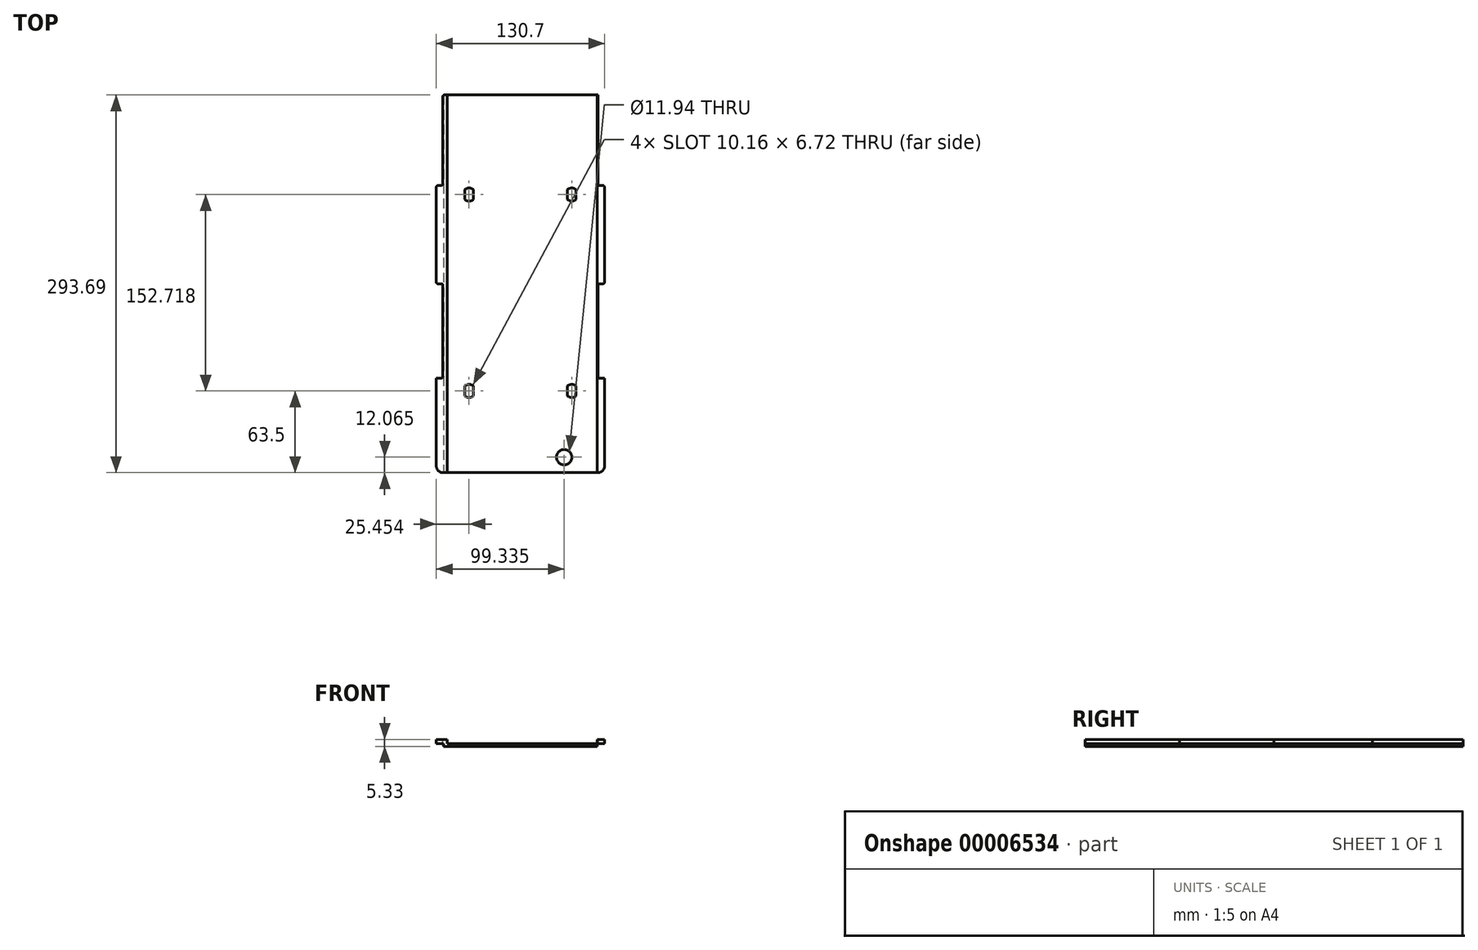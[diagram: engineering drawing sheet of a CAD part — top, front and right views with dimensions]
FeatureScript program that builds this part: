
annotation { "Feature Type Name" : "Feature", "Feature Type Description" : "" }
export const myFeature = defineFeature(function(context is Context, id is Id, definition is map)
    precondition{}
    {
        {
            var Q0;
            Q0=qCreatedBy(makeId("Front.planeOp"),FACE);
            var sketch = newSketch(context, id + "F0", { "sketchPlane" : qUnion([Q0])});
            skLineSegment(sketch, "E0.bottom", {"start": v(0, 0) * mm, "end": v(119.38, 0) * mm});
            skLineSegment(sketch, "E0.top", {"start": v(0, 2.16) * mm, "end": v(119.38, 2.16) * mm});
            skLineSegment(sketch, "E0.left", {"start": v(0, 0) * mm, "end": v(0, 2.16) * mm});
            skLineSegment(sketch, "E0.right", {"start": v(119.38, 0) * mm, "end": v(119.38, 2.16) * mm});
            skLineSegment(sketch, "E1", {"start": v(2.72, 2.16) * mm, "end": v(2.72, 5.33) * mm});
            skLineSegment(sketch, "E2", {"start": v(2.72, 5.33) * mm, "end": v(0, 5.33) * mm});
            skLineSegment(sketch, "E3", {"start": v(0, 5.33) * mm, "end": v(0, 2.16) * mm});
            skLineSegment(sketch, "E4.bottom", {"start": v(119.38, 2.16) * mm, "end": v(116.66, 2.16) * mm});
            skLineSegment(sketch, "E4.top", {"start": v(119.38, 5.33) * mm, "end": v(116.66, 5.33) * mm});
            skLineSegment(sketch, "E4.left", {"start": v(119.38, 2.16) * mm, "end": v(119.38, 5.33) * mm});
            skLineSegment(sketch, "E4.right", {"start": v(116.66, 2.16) * mm, "end": v(116.66, 5.33) * mm});
            skLineSegment(sketch, "E5.bottom", {"start": v(119.38, 5.33) * mm, "end": v(125.04, 5.33) * mm});
            skLineSegment(sketch, "E5.top", {"start": v(119.38, 2.16) * mm, "end": v(125.04, 2.16) * mm});
            skLineSegment(sketch, "E5.left", {"start": v(119.38, 5.33) * mm, "end": v(119.38, 2.16) * mm});
            skLineSegment(sketch, "E5.right", {"start": v(125.04, 5.33) * mm, "end": v(125.04, 2.16) * mm});
            skLineSegment(sketch, "E6.bottom", {"start": v(0, 5.33) * mm, "end": v(-5.66, 5.33) * mm});
            skLineSegment(sketch, "E6.top", {"start": v(0, 2.16) * mm, "end": v(-5.66, 2.16) * mm});
            skLineSegment(sketch, "E6.right", {"start": v(-5.66, 5.33) * mm, "end": v(-5.66, 2.16) * mm});
            skSolve(sketch);
        }
        {
            var Q0;
            Q0=makeQuery(id+"F0.imprint","IMPRINT",FACE,{"disambiguationData":[TD([[makeQuery(id+"F0.imprint","IMPRINT",EDGE,{"derivedFrom":sQuery(id+"F0.wireOp",EDGE,"E5.bottom")}),-1.0]])]});
            var Q1;
            Q1=makeQuery(id+"F0.imprint","IMPRINT",FACE,{"disambiguationData":[TD([[makeQuery(id+"F0.imprint","IMPRINT",EDGE,{"derivedFrom":sQuery(id+"F0.wireOp",EDGE,"E6.bottom")}),1.0]])]});
            var Q2;
            Q2=makeQuery(id+"F0.imprint","IMPRINT",FACE,{"disambiguationData":[TD([[makeQuery(id+"F0.imprint","IMPRINT",EDGE,{"derivedFrom":sQuery(id+"F0.wireOp",EDGE,"E0.bottom")}),1.0]])]});
            var Q3;
            {var subQ1=sQuery(id+"F0.wireOp",EDGE,"E1");Q3=makeQuery(id+"F0.imprint","IMPRINT",FACE,{"disambiguationData":[TD([[makeQuery(id+"F0.imprint","IMPRINT",EDGE,{"derivedFrom":subQ1}),1.0]])]});}
            var Q4;
            Q4=makeQuery(id+"F0.imprint","IMPRINT",FACE,{"disambiguationData":[TD([[makeQuery(id+"F0.imprint","IMPRINT",EDGE,{"derivedFrom":sQuery(id+"F0.wireOp",EDGE,"E4.bottom")}),-1.0]])]});
            extrude(context, id + "F1", {"entities" : qUnion([Q0, Q1, Q2, Q3, Q4]), "oppositeDirection" : true, "depth" : 293.7 * mm});
        }
        {
            var Q0;
            Q0=makeQuery(id+"F1.opExtrude","CAP_EDGE",EDGE,{"disambiguationData":[OSD([sQuery(id+"F0.wireOp",EDGE,"E5.right")])],"isStart":true});
            var Q1;
            Q1=makeQuery(id+"F1.opExtrude","CAP_EDGE",EDGE,{"disambiguationData":[OSD([sQuery(id+"F0.wireOp",EDGE,"E6.right")])],"isStart":true});
            var Q2;
            Q2=makeQuery(id+"F1.opExtrude","CAP_EDGE",EDGE,{"disambiguationData":[OSD([sQuery(id+"F0.wireOp",EDGE,"E5.right")])],"isStart":false});
            var Q3;
            Q3=makeQuery(id+"F1.opExtrude","CAP_EDGE",EDGE,{"disambiguationData":[OSD([sQuery(id+"F0.wireOp",EDGE,"E6.right")])],"isStart":false});
            fillet(context, id + "F2", {"entities" : qUnion([Q0, Q1, Q2, Q3]), "radius" : 5.08 * mm, "tangentPropagation" : true, "allowEdgeOverflow" : false});
        }
        {
            var Q0;
            Q0=makeQuery(id+"F1.opExtrude","SWEPT_FACE",FACE,{"disambiguationData":[OSD([sQuery(id+"F0.wireOp",EDGE,"E0.top")])]});
            var sketch = newSketch(context, id + "F3", { "sketchPlane" : qUnion([Q0])});
            skCircle(sketch, "E7", {"center": v(93.68, 12.06) * mm, "radius": 5.97 * mm});
            skSolve(sketch);
        }
        {
            var Q0;
            Q0=makeQuery(id+"F3.imprint","IMPRINT",FACE,{"disambiguationData":[TD([[makeQuery(id+"F3.imprint","IMPRINT",EDGE,{"derivedFrom":sQuery(id+"F3.wireOp",EDGE,"E7")}),1.0]])]});
            extrude(context, id + "F4", {"entities" : qUnion([Q0]), "operationType" : NewBodyOperationType.REMOVE, "endBound" : BoundingType.THROUGH_ALL, "oppositeDirection" : true, "depth" : 25.4 * mm});
        }
        {
            var Q0;
            Q0=makeQuery(id+"F1.opExtrude","SWEPT_FACE",FACE,{"disambiguationData":[OSD([sQuery(id+"F0.wireOp",EDGE,"E0.top")])]});
            var sketch = newSketch(context, id + "F5", { "sketchPlane" : qUnion([Q0])});
            skArc(sketch, "E8", {"start": v(16.43, 59.69) * mm, "mid": v(19.8, 58.42) * mm, "end": v(23.15, 59.69) * mm});
            skArc(sketch, "E9", {"start": v(96.23, 59.69) * mm, "mid": v(99.59, 58.42) * mm, "end": v(102.95, 59.69) * mm});
            skArc(sketch, "E10", {"start": v(96.23, 212.4) * mm, "mid": v(99.59, 211.14) * mm, "end": v(102.95, 212.4) * mm});
            skArc(sketch, "E11", {"start": v(16.43, 212.4) * mm, "mid": v(19.8, 211.14) * mm, "end": v(23.15, 212.4) * mm});
            skLineSegment(sketch, "E12", {"start": v(23.15, 59.69) * mm, "end": v(23.15, 67.3) * mm});
            skLineSegment(sketch, "E13", {"start": v(16.43, 67.31) * mm, "end": v(16.43, 59.69) * mm});
            skLineSegment(sketch, "E14", {"start": v(16.43, 212.4) * mm, "end": v(16.43, 220.03) * mm});
            skLineSegment(sketch, "E15", {"start": v(23.15, 212.4) * mm, "end": v(23.15, 220.03) * mm});
            skLineSegment(sketch, "E16", {"start": v(96.23, 212.4) * mm, "end": v(96.23, 220.03) * mm});
            skLineSegment(sketch, "E17", {"start": v(102.95, 212.4) * mm, "end": v(102.95, 220.03) * mm});
            skLineSegment(sketch, "E18", {"start": v(96.23, 59.69) * mm, "end": v(96.23, 67.31) * mm});
            skLineSegment(sketch, "E19", {"start": v(102.95, 59.69) * mm, "end": v(102.95, 67.31) * mm});
            skArc(sketch, "E20.trimOffspring", {"start": v(23.15, 67.3) * mm, "mid": v(19.8, 68.58) * mm, "end": v(16.43, 67.31) * mm});
            skArc(sketch, "E21.trimOffspring", {"start": v(23.15, 220.03) * mm, "mid": v(19.8, 221.3) * mm, "end": v(16.43, 220.03) * mm});
            skArc(sketch, "E22.trimOffspring", {"start": v(102.95, 220.03) * mm, "mid": v(99.59, 221.3) * mm, "end": v(96.23, 220.03) * mm});
            skArc(sketch, "E23.trimOffspring", {"start": v(102.95, 67.31) * mm, "mid": v(99.59, 68.58) * mm, "end": v(96.23, 67.3) * mm});
            skSolve(sketch);
        }
        {
            var Q0;
            Q0=makeQuery(id+"F5.imprint","IMPRINT",FACE,{"disambiguationData":[TD([[makeQuery(id+"F5.imprint","IMPRINT",EDGE,{"derivedFrom":sQuery(id+"F5.wireOp",EDGE,"E8")}),1.0]])]});
            var Q1;
            Q1=makeQuery(id+"F5.imprint","IMPRINT",FACE,{"disambiguationData":[TD([[makeQuery(id+"F5.imprint","IMPRINT",EDGE,{"derivedFrom":sQuery(id+"F5.wireOp",EDGE,"E9")}),1.0]])]});
            var Q2;
            Q2=makeQuery(id+"F5.imprint","IMPRINT",FACE,{"disambiguationData":[TD([[makeQuery(id+"F5.imprint","IMPRINT",EDGE,{"derivedFrom":sQuery(id+"F5.wireOp",EDGE,"E11")}),1.0]])]});
            var Q3;
            Q3=makeQuery(id+"F5.imprint","IMPRINT",FACE,{"disambiguationData":[TD([[makeQuery(id+"F5.imprint","IMPRINT",EDGE,{"derivedFrom":sQuery(id+"F5.wireOp",EDGE,"E10")}),1.0]])]});
            extrude(context, id + "F6", {"entities" : qUnion([Q0, Q1, Q2, Q3]), "operationType" : NewBodyOperationType.REMOVE, "endBound" : BoundingType.THROUGH_ALL, "oppositeDirection" : true, "depth" : 25.4 * mm});
        }
        {
            var Q0;
            Q0=makeQuery(id+"F1.opExtrude","SWEPT_FACE",FACE,{"disambiguationData":[OSD([sQuery(id+"F0.wireOp",EDGE,"E2"),sQuery(id+"F0.wireOp",EDGE,"E6.bottom")])]});
            var sketch = newSketch(context, id + "F7", { "sketchPlane" : qUnion([Q0])});
            skLineSegment(sketch, "E24", {"start": v(-5.66, 146.84) * mm, "end": v(125.04, 146.84) * mm, "construction": true});
            skLineSegment(sketch, "E25", {"start": v(59.69, 146.84) * mm, "end": v(59.69, 299.61) * mm, "construction": true});
            skLineSegment(sketch, "E26", {"start": v(59.69, 223.23) * mm, "end": v(-5.66, 223.23) * mm, "construction": true});
            skLineSegment(sketch, "E27.bottom", {"start": v(-5.66, 223.23) * mm, "end": v(-0.58, 223.23) * mm});
            skLineSegment(sketch, "E27.top", {"start": v(-5.66, 293.69) * mm, "end": v(-0.58, 293.69) * mm});
            skLineSegment(sketch, "E27.left", {"start": v(-5.66, 223.23) * mm, "end": v(-5.66, 293.69) * mm});
            skLineSegment(sketch, "E27.right", {"start": v(-0.58, 223.23) * mm, "end": v(-0.58, 293.69) * mm});
            skLineSegment(sketch, "E28.0.MirrorCS", {"start": v(119.96, 223.23) * mm, "end": v(119.96, 293.69) * mm});
            skLineSegment(sketch, "E29.0.MirrorCS", {"start": v(125.04, 223.23) * mm, "end": v(119.96, 223.23) * mm});
            skLineSegment(sketch, "E30.0.MirrorCS", {"start": v(125.04, 223.23) * mm, "end": v(125.04, 293.69) * mm});
            skLineSegment(sketch, "E31.0.MirrorCS", {"start": v(125.04, 293.69) * mm, "end": v(119.96, 293.69) * mm});
            skLineSegment(sketch, "E32", {"start": v(59.69, 146.84) * mm, "end": v(59.7, 0) * mm, "construction": true});
            skLineSegment(sketch, "E33", {"start": v(59.69, 73.42) * mm, "end": v(-5.66, 73.42) * mm, "construction": true});
            skLineSegment(sketch, "E34.bottom", {"start": v(-5.66, 73.42) * mm, "end": v(-0.58, 73.42) * mm});
            skLineSegment(sketch, "E34.top", {"start": v(-5.66, 146.84) * mm, "end": v(-0.58, 146.84) * mm});
            skLineSegment(sketch, "E34.left", {"start": v(-5.66, 73.42) * mm, "end": v(-5.66, 146.84) * mm});
            skLineSegment(sketch, "E34.right", {"start": v(-0.58, 73.42) * mm, "end": v(-0.58, 146.84) * mm});
            skLineSegment(sketch, "E35.0.MirrorCS", {"start": v(119.96, 73.42) * mm, "end": v(119.96, 146.84) * mm});
            skLineSegment(sketch, "E36.0.MirrorCS", {"start": v(125.04, 73.42) * mm, "end": v(119.96, 73.42) * mm});
            skLineSegment(sketch, "E37.0.MirrorCS", {"start": v(125.04, 73.42) * mm, "end": v(125.04, 146.84) * mm});
            skLineSegment(sketch, "E38.0.MirrorCS", {"start": v(125.04, 146.84) * mm, "end": v(119.96, 146.84) * mm});
            skSolve(sketch);
        }
        {
            var Q0;
            Q0=makeQuery(id+"F7.imprint","IMPRINT",FACE,{"disambiguationData":[TD([[makeQuery(id+"F7.imprint","IMPRINT",EDGE,{"derivedFrom":sQuery(id+"F7.wireOp",EDGE,"E34.bottom")}),1.0]])]});
            var Q1;
            {var subQ4=sQuery(id+"F7.wireOp",EDGE,"E27.bottom");Q1=makeQuery(id+"F7.imprint","IMPRINT",FACE,{"disambiguationData":[TD([[makeQuery(id+"F7.imprint","IMPRINT",EDGE,{"derivedFrom":subQ4}),1.0]])]});}
            var Q2;
            Q2=makeQuery(id+"F7.imprint","IMPRINT",FACE,{"disambiguationData":[TD([[makeQuery(id+"F7.imprint","IMPRINT",EDGE,{"derivedFrom":sQuery(id+"F7.wireOp",EDGE,"E28.0.MirrorCS")}),-1.0]])]});
            var Q3;
            Q3=makeQuery(id+"F7.imprint","IMPRINT",FACE,{"disambiguationData":[TD([[makeQuery(id+"F7.imprint","IMPRINT",EDGE,{"derivedFrom":sQuery(id+"F7.wireOp",EDGE,"E35.0.MirrorCS")}),-1.0]])]});
            extrude(context, id + "F8", {"entities" : qUnion([Q0, Q1, Q2, Q3]), "operationType" : NewBodyOperationType.REMOVE, "oppositeDirection" : true, "depth" : 25.4 * mm});
        }
        {
            var Q0;
            Q0=makeQuery(id+"F8.boolean.opBoolean","COPY",EDGE,{"derivedFrom":makeQuery(id+"F8.opExtrude","SWEPT_EDGE",EDGE,{"disambiguationData":[OSD([sQuery(id+"F7.wireOp",EDGE,"E36.0.MirrorCS"),sQuery(id+"F7.wireOp",EDGE,"E37.0.MirrorCS")])]})});
            var Q1;
            Q1=makeQuery(id+"F8.boolean.opBoolean","COPY",EDGE,{"derivedFrom":makeQuery(id+"F8.opExtrude","SWEPT_EDGE",EDGE,{"disambiguationData":[OSD([sQuery(id+"F7.wireOp",EDGE,"E35.0.MirrorCS"),sQuery(id+"F7.wireOp",EDGE,"E38.0.MirrorCS")])]})});
            var Q2;
            Q2=makeQuery(id+"F8.boolean.opBoolean","COPY",EDGE,{"derivedFrom":makeQuery(id+"F8.opExtrude","SWEPT_EDGE",EDGE,{"disambiguationData":[OSD([sQuery(id+"F7.wireOp",EDGE,"E37.0.MirrorCS"),sQuery(id+"F7.wireOp",EDGE,"E38.0.MirrorCS")])]})});
            var Q3;
            Q3=makeQuery(id+"F8.boolean.opBoolean","COPY",EDGE,{"derivedFrom":makeQuery(id+"F8.opExtrude","SWEPT_EDGE",EDGE,{"disambiguationData":[OSD([sQuery(id+"F7.wireOp",EDGE,"E29.0.MirrorCS"),sQuery(id+"F7.wireOp",EDGE,"E30.0.MirrorCS")])]})});
            var Q4;
            Q4=makeQuery(id+"F8.boolean.opBoolean","COPY",EDGE,{"derivedFrom":makeQuery(id+"F8.opExtrude","SWEPT_EDGE",EDGE,{"disambiguationData":[OSD([sQuery(id+"F7.wireOp",EDGE,"E28.0.MirrorCS"),sQuery(id+"F7.wireOp",EDGE,"E29.0.MirrorCS")])]})});
            var Q5;
            {var subQ0=sQuery(id+"F0.wireOp",EDGE,"E5.right");Q5=makeQuery(id+"F8.boolean.opBoolean","MERGE",EDGE,{"derivedFrom":[makeQuery(id+"F2.opFillet","BLEND_EDGE",EDGE,{"blendedFrom":[makeQuery(id+"F1.opExtrude","CAP_EDGE",EDGE,{"disambiguationData":[OSD([subQ0])],"isStart":false}),makeQuery(id+"F1.opExtrude","CAP_FACE",FACE,{"disambiguationData":[OSD([sQuery(id+"F0.wireOp",EDGE,"E0.bottom"),sQuery(id+"F0.wireOp",EDGE,"E0.top"),sQuery(id+"F0.wireOp",EDGE,"E0.left"),sQuery(id+"F0.wireOp",EDGE,"E0.right"),sQuery(id+"F0.wireOp",EDGE,"E1"),sQuery(id+"F0.wireOp",EDGE,"E2"),sQuery(id+"F0.wireOp",EDGE,"E4.top"),sQuery(id+"F0.wireOp",EDGE,"E4.right"),sQuery(id+"F0.wireOp",EDGE,"E5.bottom"),sQuery(id+"F0.wireOp",EDGE,"E5.top"),subQ0,sQuery(id+"F0.wireOp",EDGE,"E6.bottom"),sQuery(id+"F0.wireOp",EDGE,"E6.top"),sQuery(id+"F0.wireOp",EDGE,"E6.right")])],"isStart":false})],"blendedInto":[makeQuery(id+"F1.opExtrude","CAP_FACE",FACE,{"disambiguationData":[OSD([sQuery(id+"F0.wireOp",EDGE,"E0.bottom"),sQuery(id+"F0.wireOp",EDGE,"E0.top"),sQuery(id+"F0.wireOp",EDGE,"E0.left"),sQuery(id+"F0.wireOp",EDGE,"E0.right"),sQuery(id+"F0.wireOp",EDGE,"E1"),sQuery(id+"F0.wireOp",EDGE,"E2"),sQuery(id+"F0.wireOp",EDGE,"E4.top"),sQuery(id+"F0.wireOp",EDGE,"E4.right"),sQuery(id+"F0.wireOp",EDGE,"E5.bottom"),sQuery(id+"F0.wireOp",EDGE,"E5.top"),subQ0,sQuery(id+"F0.wireOp",EDGE,"E6.bottom"),sQuery(id+"F0.wireOp",EDGE,"E6.top"),sQuery(id+"F0.wireOp",EDGE,"E6.right")])],"isStart":false})]}),makeQuery(id+"F8.opExtrude","SWEPT_EDGE",EDGE,{"disambiguationData":[OSD([sQuery(id+"F7.wireOp",EDGE,"E28.0.MirrorCS"),sQuery(id+"F7.wireOp",EDGE,"E31.0.MirrorCS")])]})]});}
            var Q6;
            Q6=makeQuery(id+"F8.boolean.opBoolean","COPY",EDGE,{"derivedFrom":makeQuery(id+"F8.opExtrude","SWEPT_EDGE",EDGE,{"disambiguationData":[OSD([sQuery(id+"F7.wireOp",EDGE,"E35.0.MirrorCS"),sQuery(id+"F7.wireOp",EDGE,"E36.0.MirrorCS")])]})});
            var Q7;
            Q7=makeQuery(id+"F8.boolean.opBoolean","COPY",EDGE,{"derivedFrom":makeQuery(id+"F8.opExtrude","SWEPT_EDGE",EDGE,{"disambiguationData":[OSD([sQuery(id+"F0.wireOp",EDGE,"E6.bottom"),sQuery(id+"F0.wireOp",EDGE,"E6.right"),sQuery(id+"F7.wireOp",EDGE,"E34.bottom"),sQuery(id+"F7.wireOp",EDGE,"E34.left")])]})});
            var Q8;
            Q8=makeQuery(id+"F8.boolean.opBoolean","COPY",EDGE,{"derivedFrom":makeQuery(id+"F8.opExtrude","SWEPT_EDGE",EDGE,{"disambiguationData":[OSD([sQuery(id+"F7.wireOp",EDGE,"E34.bottom"),sQuery(id+"F7.wireOp",EDGE,"E34.right")])]})});
            var Q9;
            Q9=makeQuery(id+"F8.boolean.opBoolean","COPY",EDGE,{"derivedFrom":makeQuery(id+"F8.opExtrude","SWEPT_EDGE",EDGE,{"disambiguationData":[OSD([sQuery(id+"F7.wireOp",EDGE,"E34.top"),sQuery(id+"F7.wireOp",EDGE,"E34.right")])]})});
            var Q10;
            Q10=makeQuery(id+"F8.boolean.opBoolean","COPY",EDGE,{"derivedFrom":makeQuery(id+"F8.opExtrude","SWEPT_EDGE",EDGE,{"disambiguationData":[OSD([sQuery(id+"F0.wireOp",EDGE,"E6.bottom"),sQuery(id+"F0.wireOp",EDGE,"E6.right"),sQuery(id+"F7.wireOp",EDGE,"E34.top"),sQuery(id+"F7.wireOp",EDGE,"E34.left")])]})});
            var Q11;
            Q11=makeQuery(id+"F8.boolean.opBoolean","COPY",EDGE,{"derivedFrom":makeQuery(id+"F8.opExtrude","SWEPT_EDGE",EDGE,{"disambiguationData":[OSD([sQuery(id+"F0.wireOp",EDGE,"E6.bottom"),sQuery(id+"F0.wireOp",EDGE,"E6.right"),sQuery(id+"F7.wireOp",EDGE,"E27.bottom"),sQuery(id+"F7.wireOp",EDGE,"E27.left")])]})});
            var Q12;
            Q12=makeQuery(id+"F8.boolean.opBoolean","COPY",EDGE,{"derivedFrom":makeQuery(id+"F8.opExtrude","SWEPT_EDGE",EDGE,{"disambiguationData":[OSD([sQuery(id+"F7.wireOp",EDGE,"E27.bottom"),sQuery(id+"F7.wireOp",EDGE,"E27.right")])]})});
            var Q13;
            {var subQ0=sQuery(id+"F0.wireOp",EDGE,"E6.right");var subQ1=sQuery(id+"F0.wireOp",EDGE,"E2");var subQ2=sQuery(id+"F0.wireOp",EDGE,"E6.bottom");Q13=makeQuery(id+"F8.boolean.opBoolean","MERGE",EDGE,{"derivedFrom":[makeQuery(id+"F2.opFillet","BLEND_EDGE",EDGE,{"blendedFrom":[makeQuery(id+"F1.opExtrude","CAP_EDGE",EDGE,{"disambiguationData":[OSD([subQ0])],"isStart":false}),makeQuery(id+"F1.opExtrude","CAP_FACE",FACE,{"disambiguationData":[OSD([sQuery(id+"F0.wireOp",EDGE,"E0.bottom"),sQuery(id+"F0.wireOp",EDGE,"E0.top"),sQuery(id+"F0.wireOp",EDGE,"E0.left"),sQuery(id+"F0.wireOp",EDGE,"E0.right"),sQuery(id+"F0.wireOp",EDGE,"E1"),subQ1,sQuery(id+"F0.wireOp",EDGE,"E4.top"),sQuery(id+"F0.wireOp",EDGE,"E4.right"),sQuery(id+"F0.wireOp",EDGE,"E5.bottom"),sQuery(id+"F0.wireOp",EDGE,"E5.top"),sQuery(id+"F0.wireOp",EDGE,"E5.right"),subQ2,sQuery(id+"F0.wireOp",EDGE,"E6.top"),subQ0])],"isStart":false})],"blendedInto":[makeQuery(id+"F1.opExtrude","CAP_FACE",FACE,{"disambiguationData":[OSD([sQuery(id+"F0.wireOp",EDGE,"E0.bottom"),sQuery(id+"F0.wireOp",EDGE,"E0.top"),sQuery(id+"F0.wireOp",EDGE,"E0.left"),sQuery(id+"F0.wireOp",EDGE,"E0.right"),sQuery(id+"F0.wireOp",EDGE,"E1"),subQ1,sQuery(id+"F0.wireOp",EDGE,"E4.top"),sQuery(id+"F0.wireOp",EDGE,"E4.right"),sQuery(id+"F0.wireOp",EDGE,"E5.bottom"),sQuery(id+"F0.wireOp",EDGE,"E5.top"),sQuery(id+"F0.wireOp",EDGE,"E5.right"),subQ2,sQuery(id+"F0.wireOp",EDGE,"E6.top"),subQ0])],"isStart":false})]}),makeQuery(id+"F8.opExtrude","SWEPT_EDGE",EDGE,{"disambiguationData":[OSD([subQ1,subQ2,subQ0,sQuery(id+"F7.wireOp",EDGE,"E27.top"),sQuery(id+"F7.wireOp",EDGE,"E27.right")])]})]});}
            fillet(context, id + "F9", {"entities" : qUnion([Q0, Q1, Q2, Q3, Q4, Q5, Q6, Q7, Q8, Q9, Q10, Q11, Q12, Q13]), "radius" : 1.27 * mm, "tangentPropagation" : true, "allowEdgeOverflow" : false});
        }
    });
